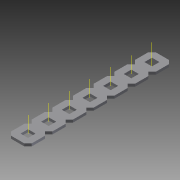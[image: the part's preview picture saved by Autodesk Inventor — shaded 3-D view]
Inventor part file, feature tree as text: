
AUTODESK INVENTOR PART (.ipt)
format: ipt  version: 2015 (Build 190159000, 159)  size: 1,128,448 bytes
history: native  units: in
note: dims shown in document units (in); Inventor stores cm internally (conversion verified against a paired STEP export)
features: other x16, extrude x2, pattern_linear x1, imported_body x1
ambient origin geometry x8: Origin, YZ Plane, XZ Plane, XY Plane, X Axis, Y Axis, Z Axis, Center Point
bodies: Body1 (feature_tree)
feature tree (20):
  other  "Diamond-Pattern"
  other  "Plate"
  extrude  "length cut"  TaperAngle=0.0deg  [1 undecoded]
  extrude  "width cut"  TaperAngle=0.0deg  [1 undecoded]
  other  "constraint axis"
  pattern_linear  "constraint axes"  Spacing1=0.5in  [1 undecoded]
  other  "front plane"
  other  "right plane"
  imported_body  "Base1"
  other  "length profile"
  other  "width profile"
  other  "Work Point1"
  other  "back plane"
  other  "left plane"
  other  "Work Axis170"
  other  "Work Axis171"
  other  "Work Axis172"
  other  "Work Axis173"
  other  "Work Axis174"
  other  "Work Axis175"
note: 3 required parameter values undecoded (feature->parameter linkage not recoverable at this tier; creation-order binding heuristic only, values carry confidence <= 0.55)
